AUTODESK INVENTOR PART (.ipt)
format: ipt  version: 2017 (Build 210142000, 142)  size: 139,264 bytes
history: native  units: mm
features: extrude x4, sketch x4
ambient origin geometry x8: Origin, YZ Plane, XZ Plane, XY Plane, X Axis, Y Axis, Z Axis, Center Point
bodies: Solid1 (feature_tree)
feature tree (8):
  extrude  "Extrusion1"  Depth=20.25mm
  extrude  "Extrusion2"  Depth=3.565mm
  extrude  "Extrusion3"  Depth=1.5mm TaperAngle=0.0deg
  extrude  "Extrusion4"  Depth=2.5mm
  sketch  "Sketch1"  dims[d0=20.25mm d1=61.1mm]
  sketch  "Sketch2"  dims[d2=8.0mm d3=3.565mm]
  sketch  "Sketch3"  dims[d4=14.35mm d5=1.5mm d6=0.0mm]
  sketch  "Sketch4"  dims[d7=4.86mm d8=2.5mm d9=1.12mm d10=5.3mm d11=0.0mm d12=2.39mm d13=12.0mm d14=0.0mm d15=2.9mm d16=12.4mm d17=1.35mm d18=12.0mm d19=0.0mm]
